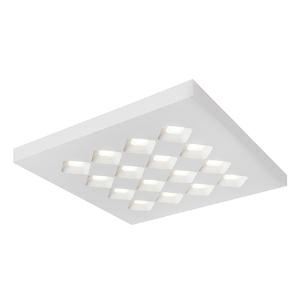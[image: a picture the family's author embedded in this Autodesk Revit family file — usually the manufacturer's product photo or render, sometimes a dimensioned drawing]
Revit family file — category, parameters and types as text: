
# Revit family: 3f_filippi_-_3f_diagon_p_soft_ugr_3f_filippi_-_12127_-_3f_diagon_p_25w-830_dali_soft_ugr_596x596
name_source: partatom
category: Lighting Fixtures
units: mm (PartAtom-declared; Revit-internal decimal feet)

## family parameters
Cut with Voids When Loaded = No
Host = Face
Light Source = No
Part Type = Normal
Room Calculation Point = No
Round Connector Dimension = Use Diameter
Shared = No

## types (1)
- 3F Filippi - 3F Dìagon P Soft UGR (1 x LED, 3495 lm, 28 W, 3000 K)
    Apparent Load = 28 VA
    Approval mark = CE
    CIE Flux Codes = 59 92 100 100 100
    Color Rendering = 80
    Color Temperature = 3000 K
    Control Gear = Electronic transformer
    Default Elevation = 1800 mm
    Description = ILLUMINOTECHNICAL
Luminous efficiency 100% (DLOR 100%, ULOR 0%).
Initial luminous flux of the luminaire 3495 lm.
Direct symmetric distribution.
Installation Interdistance Transv.D = 1.23 x hu - Long.D = 1.23 x hu.
Average luminance <3000 cd/m² for radial angles >65°.
Tabular UGR (CIE 117 - 4H-8H; S=0.25H; 70/50/20): RUG 18.6 - 18.5.
Beam angle: 102° - 101°.
Luminous efficacy 125 lm/W.
Lifetime (L95/B10): 30000 h. (tq+25°C)
Lifetime (L90/B10): 50000 h. (tq+25°C)
Lifetime (L80/B10): 80000 h. (tq+25°C)
Lifetime (L75/B10): 100000 h. (tq+25°C)
Sudden decreased luminous flux after 50000 hours: 0% (C0).
Photobiological safety in compliance with IEC/TR 62778: RG0 risk exempt, (IEC 62471).
In compliance with IEC/EN 62722-2-1 - IEC/EN 62717 standards.

SOURCE
Squared LED module 25W/830.
Energy efficiency class (UE 2019/2020 - UE 2019/2015): C.
CIE 13.3 Colour rendering index: CRI >80 (R9 <50%).
IES TM-30 Fidelity Index: Rf = 84 Rg = 95.
CCT nominal colour temperature 3000 K.
Colour initial tolerance (MacAdam): SDCM 3.

MECHANICAL
White painted frame.
Height only 40 mm.
Housing in hot-galvanised steel, painted in white polyester.
Honeycombed diagonal screen in white anti-glare polycarbonate.
Opal methacrylate (PMMA) rhomboid lenses with differentiated, engraved and prismatic surfaces for diffused, soft lighting and excellent visual comfort.
Luminaire with limited surface temperature. - D - (EN 60598-2-24)
Dimensions: 596x596 mm, height 40 mm. Weight 5.9 kg.
IP40 protection degree.
Mechanical strength to impacts IK06 (1 joule).
Glow-wire test resistance 650°C.

ELECTRICAL
Halogen Free DALI-2, PUSH-DIM, electronic wiring 230V-50/60Hz, power factor 0.95 at full load, THD <25%, constant output current, class I, 1 driver, 1 DALI addresse.
Power of the luminaire 28 W.
ENEC - CE.
SAFE FLICKER: PstLM=<1 and SVM=<0.4 (IEC TR 61547-1 and IEC TR 63158), to ensure a more comfortable and safe light.
Luminaire compliant with EN 60598-2-22 for power supply from a centralised emergency system CPSS (Central Power Supply System), not incorporated in the luminaire - high risk areas excluded. The default power and flux are 100% in AC and 15% in DC.
Ambient temperature from 0°C to +25°C.
Temperature class T6 max 85°C.
Quick connection.
Relative humidity UR: <85%.

INSTALLATION
Ceiling.

APPLICATIONS
Environments: staterooms, with VDTs, offices.
Environments with exacting visual tasks, where diffused soft light for optimum visual comfort is required.

LIGHT MANAGEMENT
Recommended minimum setting: 10%.
The device, equipped with DALI-2 driver, can be controlled manually with 3F Easy Dim technology or automatically/manually with 3F Smart Dimming technology and/or centralised DALI systems.
DALI-2 certification guarantees interoperability with other devices with the same certification.
In electrical systems without a regulation system (manual or automatic) and DALI bus, a suitable jumper must be made on the DA-DA terminals of the appliance.

WARNING
Luminaire designed for disposal/recycling at end-of-life.
Replaceable (LED only) light source by a professional. Replaceable control gear by a professional.
    Height = 40 mm  [stored 0.131234 ft]
    Lamp = 1 x LED
    Lamp Light Flux = 3495 lm
    Lamp Power = 28 W
    Lamp count = 1
    Length = 596 mm
    Lifetime = 50000 h
    Luminous efficacy = 125 lm/W
    Manufacturer = 3F Filippi
    ModVariant = No
    Model = 3F Filippi - 12127 - 3F Diagon P 25W-830 DALI SOFT UGR 596x596
    Mounting Place = Ceiling
    Mounting Type = Surface mounted
    Number of Poles = 1
    OnlyDefault = Yes
    Power Factor = 1
    Product Name = 3F Filippi - 3F Dìagon P Soft UGR
    Product group = ceiling mounted luminaire
    ProductGroupID = 3
    Protection Class = Protection class I
    Protection Degree = IP 40
    RLX_Detail_Level = 1
    RLX_Emergency_Light_Flux = 0 lm
    RLX_Emergency_Type = 0
    RLX_Emergency_Type_DB = No
    RlxData = <blob elided: 96849 chars, md5=b68ccad2>
    Socket = socket
    Standby Power = 0 W
    System Light Flux = 3495 lm
    System Power = 28 W
    Type Comments = Product without accessories
    Type Image = 3ffilippi_3f_diagon_p_soft_ugr.jpg
    URL = http://relux.com
    VarID = ---
    Voltage = 0 V
    Weight = 0.00 kg
    Width = 596 mm

note: [stored X ft] marks values corroborated as IEEE doubles in the binary element streams (Revit-internal decimal feet)

## geometry (parser evidence)
native form markers: Blend x4, Sweep x11
no freeform markers — native parametric forms only
